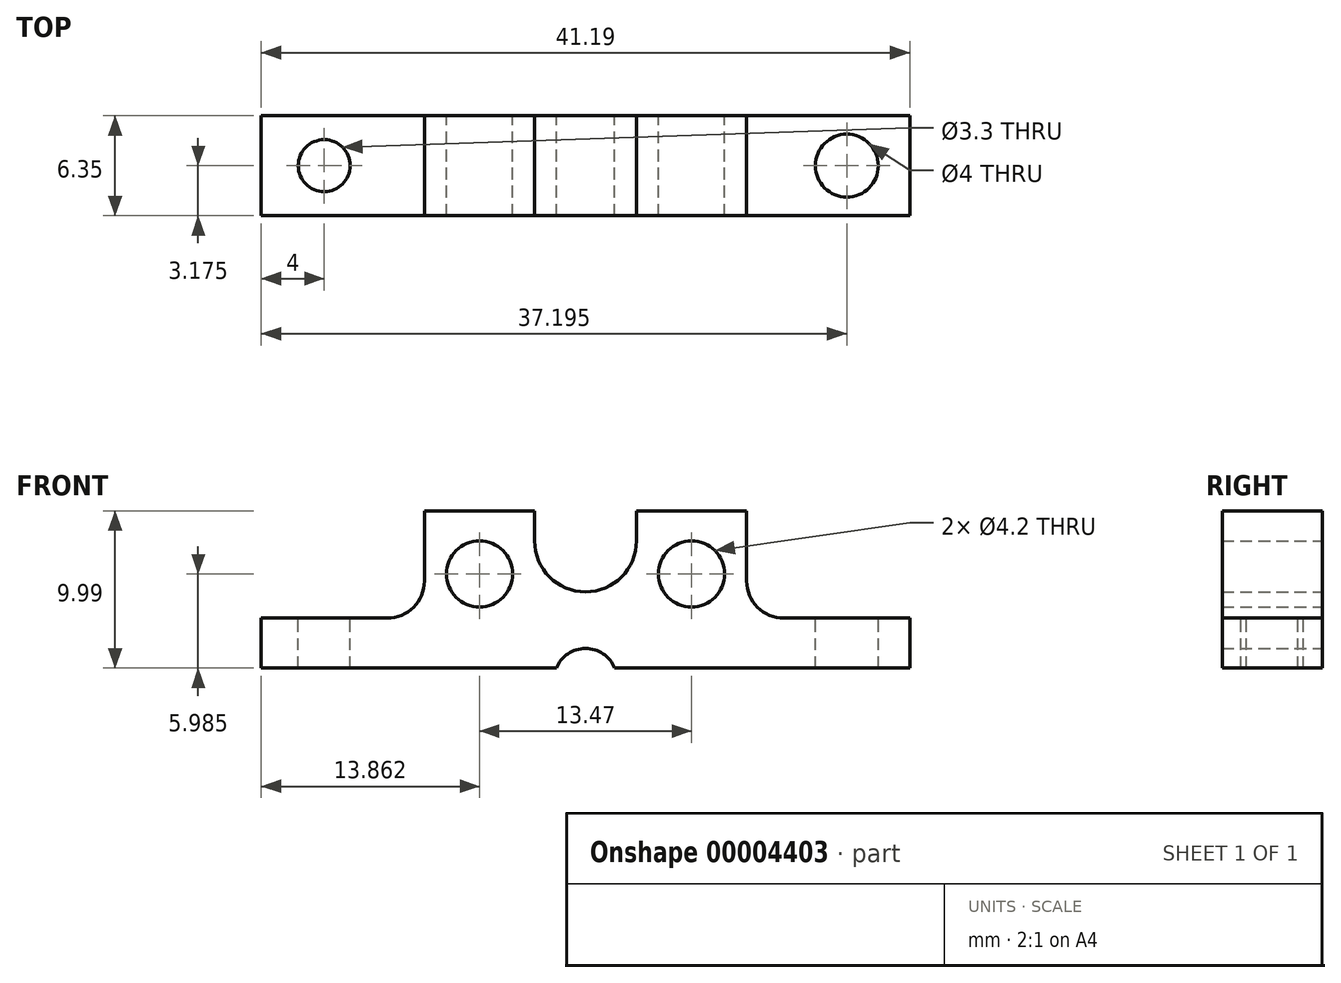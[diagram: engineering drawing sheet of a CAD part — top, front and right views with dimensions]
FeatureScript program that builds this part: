
annotation { "Feature Type Name" : "Feature", "Feature Type Description" : "" }
export const myFeature = defineFeature(function(context is Context, id is Id, definition is map)
    precondition{}
    {
        {
            var Q0;
            Q0=qCreatedBy(makeId("Front.planeOp"),FACE);
            var sketch = newSketch(context, id + "F0", { "sketchPlane" : qUnion([Q0])});
            skLineSegment(sketch, "E0", {"start": v(41.2, 0) * mm, "end": v(41.2, 3.18) * mm});
            skLineSegment(sketch, "E1", {"start": v(41.2, 3.18) * mm, "end": v(33.2, 3.18) * mm});
            skLineSegment(sketch, "E2", {"start": v(30.83, 5.54) * mm, "end": v(30.83, 9.99) * mm});
            skLineSegment(sketch, "E3", {"start": v(30.83, 9.99) * mm, "end": v(23.83, 9.99) * mm});
            skLineSegment(sketch, "E4", {"start": v(23.83, 9.99) * mm, "end": v(23.83, 8.08) * mm});
            skLineSegment(sketch, "E5", {"start": v(17.36, 8.08) * mm, "end": v(17.36, 9.99) * mm});
            skLineSegment(sketch, "E6", {"start": v(17.36, 9.99) * mm, "end": v(10.36, 9.99) * mm});
            skLineSegment(sketch, "E7", {"start": v(10.36, 9.99) * mm, "end": v(10.36, 5.54) * mm});
            skLineSegment(sketch, "E8", {"start": v(8, 3.18) * mm, "end": v(0, 3.18) * mm});
            skLineSegment(sketch, "E9", {"start": v(0, 3.18) * mm, "end": v(0, 0) * mm});
            skPoint(sketch, "E10.visualSharp", {"position": v(30.83, 3.18) * mm});
            skArc(sketch, "E10.filletArc", {"start": v(30.83, 5.54) * mm, "mid": v(31.52, 3.87) * mm, "end": v(33.2, 3.18) * mm});
            skPoint(sketch, "E11.visualSharp", {"position": v(10.36, 3.18) * mm});
            skArc(sketch, "E11.filletArc", {"start": v(8, 3.18) * mm, "mid": v(9.67, 3.87) * mm, "end": v(10.36, 5.54) * mm});
            skCircle(sketch, "E12", {"center": v(13.86, 5.99) * mm, "radius": 2.1 * mm});
            skCircle(sketch, "E13", {"center": v(27.33, 5.99) * mm, "radius": 2.1 * mm});
            skLineSegment(sketch, "E14", {"start": v(13.86, 5.99) * mm, "end": v(20.6, -0.75) * mm, "construction": true});
            skLineSegment(sketch, "E15", {"start": v(20.6, -0.75) * mm, "end": v(27.33, 5.99) * mm, "construction": true});
            skPoint(sketch, "E16", {"position": v(13.86, 9.99) * mm});
            skPoint(sketch, "E17", {"position": v(27.33, 9.99) * mm});
            skArc(sketch, "E18", {"start": v(22.45, 0) * mm, "mid": v(20.6, 1.25) * mm, "end": v(18.74, 0) * mm});
            skLineSegment(sketch, "E19", {"start": v(0, 0) * mm, "end": v(18.74, 0) * mm});
            skLineSegment(sketch, "E20", {"start": v(22.45, 0) * mm, "end": v(41.2, 0) * mm});
            skCircle(sketch, "E21", {"center": v(13.86, 5.99) * mm, "radius": 2.5 * mm, "construction": true});
            skArc(sketch, "E22", {"start": v(17.36, 8.08) * mm, "mid": v(20.6, 4.84) * mm, "end": v(23.83, 8.08) * mm});
            skSolve(sketch);
        }
        {
            var Q0;
            Q0 = qSketchRegion(id + "F0", true);
            extrude(context, id + "F1", {"entities" : qUnion([Q0]), "depth" : 6.35 * mm});
        }
        {
            var Q0;
            Q0=makeQuery(id+"F1.opExtrude","SWEPT_FACE",FACE,{"disambiguationData":[OSD([sQuery(id+"F0.wireOp",EDGE,"E8")])]});
            var sketch = newSketch(context, id + "F2", { "sketchPlane" : qUnion([Q0])});
            skLineSegment(sketch, "E23", {"start": v(0, -3.18) * mm, "end": v(4, -3.18) * mm, "construction": true});
            skLineSegment(sketch, "E24", {"start": v(4, -3.18) * mm, "end": v(4, 0) * mm, "construction": true});
            skCircle(sketch, "E25", {"center": v(4, -3.18) * mm, "radius": 1.65 * mm});
            skSolve(sketch);
        }
        {
            var Q0;
            Q0 = qSketchRegion(id + "F2", true);
            extrude(context, id + "F3", {"entities" : qUnion([Q0]), "operationType" : NewBodyOperationType.REMOVE, "endBound" : BoundingType.THROUGH_ALL, "oppositeDirection" : true, "depth" : 25.4 * mm});
        }
        {
            var Q0;
            Q0=makeQuery(id+"F1.opExtrude","SWEPT_FACE",FACE,{"disambiguationData":[OSD([sQuery(id+"F0.wireOp",EDGE,"E1")])]});
            var sketch = newSketch(context, id + "F4", { "sketchPlane" : qUnion([Q0])});
            skLineSegment(sketch, "E26", {"start": v(37.2, 0) * mm, "end": v(37.2, -3.18) * mm, "construction": true});
            skLineSegment(sketch, "E27", {"start": v(37.2, -3.18) * mm, "end": v(41.2, -3.18) * mm, "construction": true});
            skCircle(sketch, "E28", {"center": v(37.2, -3.18) * mm, "radius": 2 * mm});
            skSolve(sketch);
        }
        {
            var Q0;
            Q0=makeQuery(id+"F4.imprint","IMPRINT",FACE,{"disambiguationData":[TD([[makeQuery(id+"F4.imprint","IMPRINT",EDGE,{"derivedFrom":sQuery(id+"F4.wireOp",EDGE,"E28")}),1.0]])]});
            extrude(context, id + "F5", {"entities" : qUnion([Q0]), "operationType" : NewBodyOperationType.REMOVE, "endBound" : BoundingType.THROUGH_ALL, "oppositeDirection" : true, "depth" : 25.4 * mm});
        }
    });
